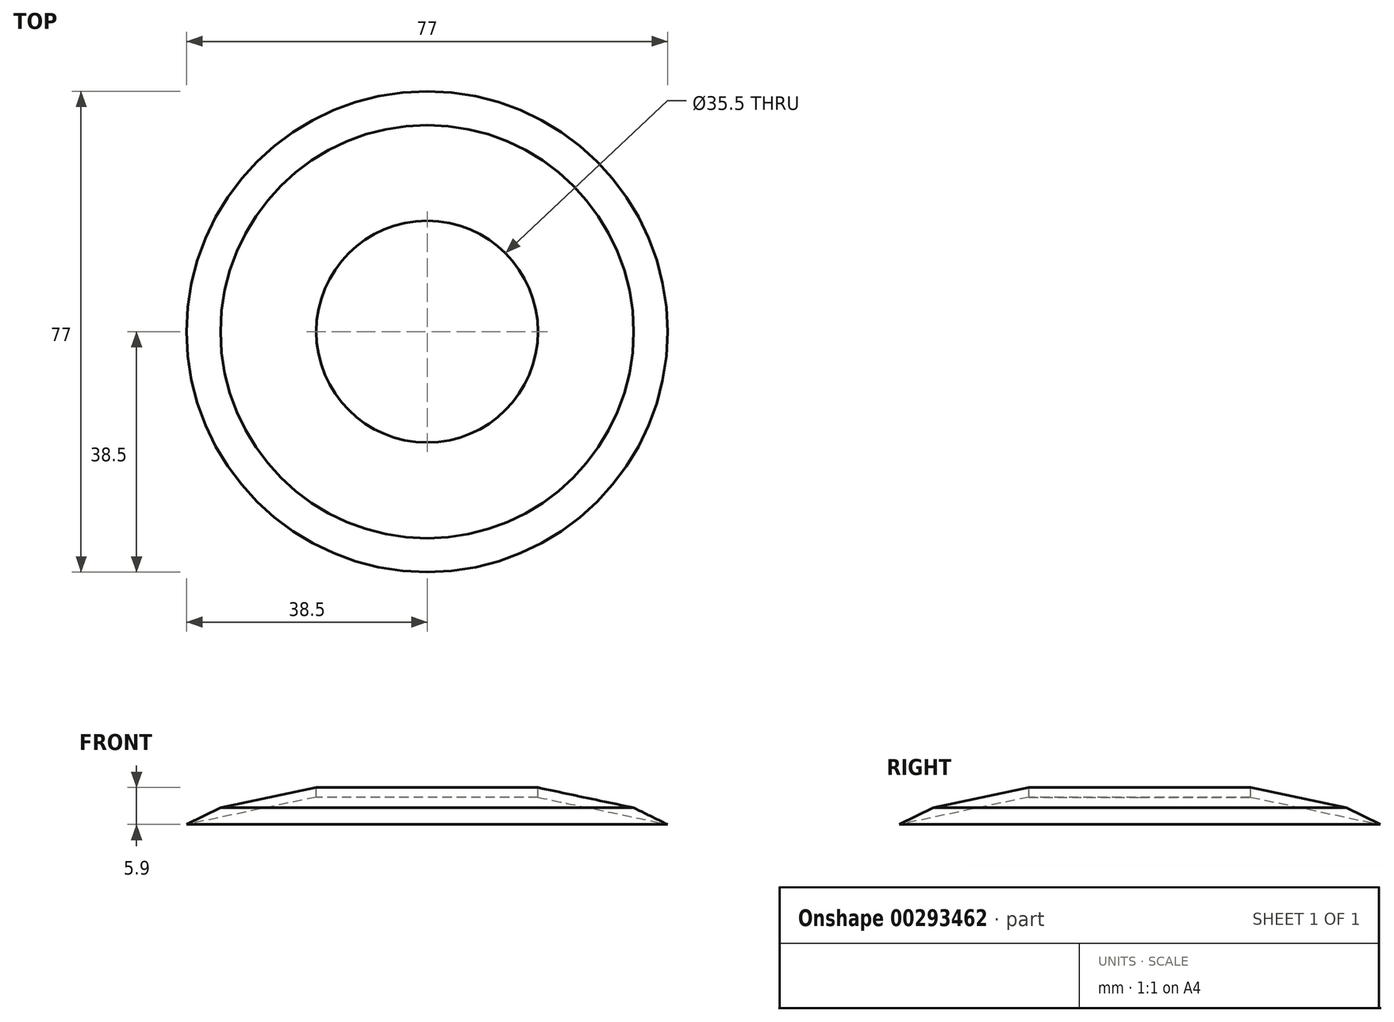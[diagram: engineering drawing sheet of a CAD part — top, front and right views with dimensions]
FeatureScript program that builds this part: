
annotation { "Feature Type Name" : "Feature", "Feature Type Description" : "" }
export const myFeature = defineFeature(function(context is Context, id is Id, definition is map)
    precondition{}
    {
        {
            var Q0;
            Q0=qCreatedBy(makeId("Front.planeOp"),FACE);
            var sketch = newSketch(context, id + "F0", { "sketchPlane" : qUnion([Q0])});
            skLineSegment(sketch, "E0", {"start": v(0, 24.37) * mm, "end": v(0, -28.76) * mm});
            skLineSegment(sketch, "E1", {"start": v(-17.75, 5.9) * mm, "end": v(-33.07, 2.68) * mm});
            skLineSegment(sketch, "E2", {"start": v(-17.75, 4.37) * mm, "end": v(-38.5, 0) * mm});
            skLineSegment(sketch, "E3", {"start": v(0, 0) * mm, "end": v(-44.9, 0) * mm, "construction": true});
            skLineSegment(sketch, "E4", {"start": v(-17.75, 5.9) * mm, "end": v(-17.75, 4.37) * mm});
            skLineSegment(sketch, "E5", {"start": v(-33.07, 2.68) * mm, "end": v(-38.5, 0) * mm});
            skLineSegment(sketch, "E6", {"start": v(0, 17.72) * mm, "end": v(0, -15.44) * mm, "construction": true});
            skSolve(sketch);
        }
        {
            var Q0;
            Q0=makeQuery(id+"F0.imprint","IMPRINT",FACE,{"disambiguationData":[TD([[makeQuery(id+"F0.imprint","IMPRINT",EDGE,{"derivedFrom":sQuery(id+"F0.wireOp",EDGE,"E1")}),1.0]])]});
            var Q1;
            Q1=sQuery(id+"F0.wireOp",EDGE,"E0");
            revolve(context, id + "F1", {"surfaceOperationType" : NewSurfaceOperationType.NEW, "entities" : qUnion([Q0]), "axis" : qUnion([Q1]), "revolveType" : RevolveType.FULL});
        }
    });
